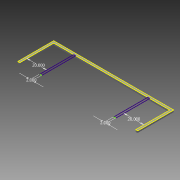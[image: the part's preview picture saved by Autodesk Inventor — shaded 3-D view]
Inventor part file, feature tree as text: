
AUTODESK INVENTOR PART (.ipt)
format: ipt  version: 2014 (Build 180170000, 170)  size: 90,112 bytes
history: native  units: in
note: dims shown in document units (in); Inventor stores cm internally (conversion verified against a paired STEP export)
features: sketch x3, extrude x2
ambient origin geometry x8: Origin, YZ Plane, XZ Plane, XY Plane, X Axis, Y Axis, Z Axis, Center Point
bodies: Solid1 (feature_tree)
feature tree (5):
  extrude  "Extrusion1"  Depth=36.0in
  extrude  "Extrusion2"  Depth=116.0in
  sketch  "Sketch3"  dims[d5=34.0in d6=17.4375in d7=0.0in d8=2.0in d9=2.0in d10=20.0in d11=20.0in]
  sketch  "Sketch1"  dims[d0=120.0in d1=36.0in]
  sketch  "Sketch2"  dims[d2=2.0in d3=0.0in d4=116.0in]
